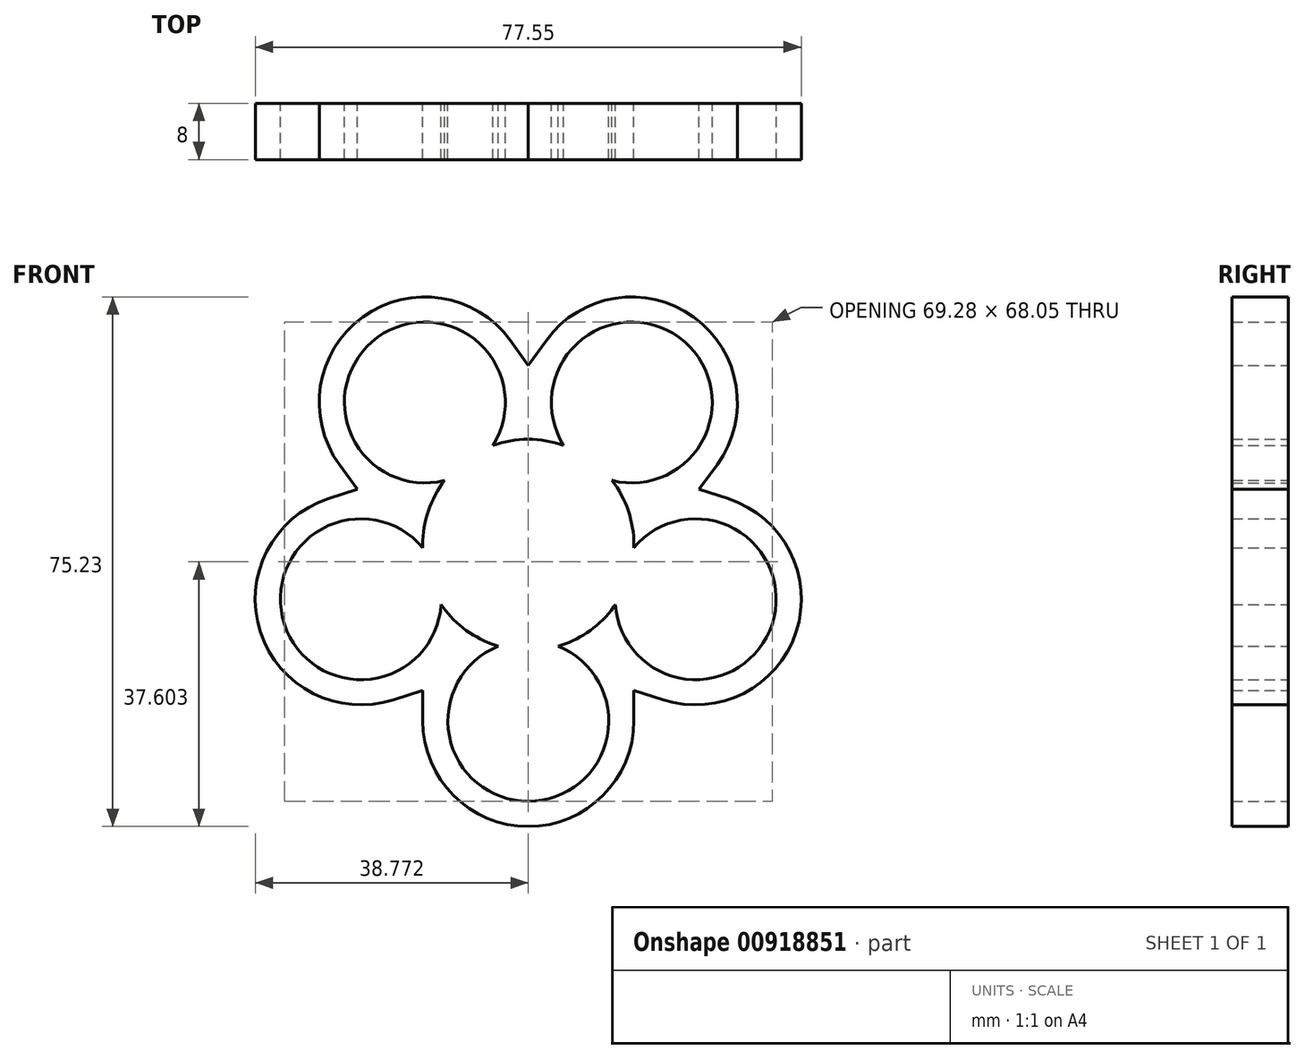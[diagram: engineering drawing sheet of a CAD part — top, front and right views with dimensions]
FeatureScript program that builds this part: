
annotation { "Feature Type Name" : "Feature", "Feature Type Description" : "" }
export const myFeature = defineFeature(function(context is Context, id is Id, definition is map)
    precondition{}
    {
        {
            var Q0;
            Q0=qCreatedBy(makeId("Front.planeOp"),FACE);
            var sketch = newSketch(context, id + "F0", { "sketchPlane" : qUnion([Q0])});
            skCircle(sketch, "E0", {"center": v(-50.1, -29.2) * mm, "radius": 11.43 * mm});
            skCircle(sketch, "E1", {"center": v(-50.1, -54.2) * mm, "radius": 11.43 * mm});
            skArc(sketch, "E2", {"start": v(-65.1, -29.2) * mm, "mid": v(-50.1, -14.2) * mm, "end": v(-35.1, -29.2) * mm});
            skArc(sketch, "E3", {"start": v(-65.1, -54.2) * mm, "mid": v(-50.1, -69.2) * mm, "end": v(-35.1, -54.2) * mm});
            skLineSegment(sketch, "E4", {"start": v(-65.1, -29.2) * mm, "end": v(-65.1, -54.2) * mm});
            skLineSegment(sketch, "E5", {"start": v(-35.1, -29.2) * mm, "end": v(-35.1, -54.2) * mm});
            skArc(sketch, "E6.1.0", {"start": v(-30.96, -51.19) * mm, "mid": v(-12.06, -41.56) * mm, "end": v(-21.69, -22.66) * mm});
            skCircle(sketch, "E6.1.1", {"center": v(-50.1, -29.2) * mm, "radius": 11.42 * mm});
            skArc(sketch, "E6.1.2", {"start": v(-54.73, -43.46) * mm, "mid": v(-64.36, -24.56) * mm, "end": v(-45.46, -14.93) * mm});
            skCircle(sketch, "E6.1.3", {"center": v(-26.32, -36.92) * mm, "radius": 11.42 * mm});
            skLineSegment(sketch, "E6.1.4", {"start": v(-54.73, -43.46) * mm, "end": v(-30.96, -51.19) * mm});
            skLineSegment(sketch, "E6.1.5", {"start": v(-45.46, -14.93) * mm, "end": v(-21.69, -22.66) * mm});
            skArc(sketch, "E6.2.0", {"start": v(-23.27, -17.79) * mm, "mid": v(-26.59, 3.16) * mm, "end": v(-47.54, -0.16) * mm});
            skArc(sketch, "E6.2.2", {"start": v(-37.96, -38.02) * mm, "mid": v(-58.92, -41.33) * mm, "end": v(-62.23, -20.38) * mm});
            skCircle(sketch, "E6.2.3", {"center": v(-35.4, -8.97) * mm, "radius": 11.43 * mm});
            skLineSegment(sketch, "E6.2.4", {"start": v(-37.96, -38.02) * mm, "end": v(-23.27, -17.79) * mm});
            skLineSegment(sketch, "E6.2.5", {"start": v(-62.23, -20.38) * mm, "end": v(-47.54, -0.16) * mm});
            skArc(sketch, "E7.2.3.0", {"start": v(-52.66, -0.16) * mm, "mid": v(-73.6, 3.16) * mm, "end": v(-76.93, -17.79) * mm});
            skArc(sketch, "E7.6.3.0", {"start": v(-37.96, -20.38) * mm, "mid": v(-41.28, -41.33) * mm, "end": v(-62.23, -38.02) * mm});
            skCircle(sketch, "E7.10.3.0", {"center": v(-64.8, -8.97) * mm, "radius": 11.43 * mm});
            skLineSegment(sketch, "E7.12.3.0", {"start": v(-37.96, -20.38) * mm, "end": v(-52.66, -0.16) * mm});
            skLineSegment(sketch, "E7.15.3.0", {"start": v(-62.23, -38.02) * mm, "end": v(-76.93, -17.79) * mm});
            skArc(sketch, "E7.2.4.0", {"start": v(-78.51, -22.66) * mm, "mid": v(-88.14, -41.56) * mm, "end": v(-69.24, -51.19) * mm});
            skArc(sketch, "E7.6.4.0", {"start": v(-54.73, -14.93) * mm, "mid": v(-35.83, -24.56) * mm, "end": v(-45.46, -43.46) * mm});
            skCircle(sketch, "E7.10.4.0", {"center": v(-73.87, -36.92) * mm, "radius": 11.43 * mm});
            skLineSegment(sketch, "E7.12.4.0", {"start": v(-54.73, -14.93) * mm, "end": v(-78.51, -22.66) * mm});
            skLineSegment(sketch, "E7.15.4.0", {"start": v(-45.46, -43.46) * mm, "end": v(-69.24, -51.19) * mm});
            skSolve(sketch);
        }
        {
            var Q0;
            Q0 = qSketchRegion(id + "F0", true);
            var Q1;
            {var subQ8=sQuery(id+"F0.wireOp",EDGE,"E2");Q1=makeQuery(id+"F0.imprint","IMPRINT",FACE,{"disambiguationData":[TD([[makeQuery(id+"F0.imprint","IMPRINT",EDGE,{"derivedFrom":subQ8}),-1.0]])]});}
            var Q2;
            Q2=makeQuery(id+"F0.imprint","IMPRINT",FACE,{"disambiguationData":[TD([[makeQuery(id+"F0.imprint","IMPRINT",EDGE,{"derivedFrom":sQuery(id+"F0.wireOp",EDGE,"E0")}),-1.0]])]});
            extrude(context, id + "F1", {"entities" : qUnion([Q0, Q1, Q2]), "depth" : 8 * mm, "offsetDistance" : 25 * mm});
        }
    });
